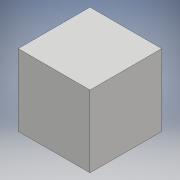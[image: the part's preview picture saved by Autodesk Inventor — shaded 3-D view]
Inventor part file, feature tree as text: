
AUTODESK INVENTOR PART (.ipt)
format: ipt  version: 2018 (Build 220112000, 112)  size: 83,968 bytes
history: native  units: mm
features: extrude x1, sketch x1
ambient origin geometry x8: Origin, YZ Plane, XZ Plane, XY Plane, X Axis, Y Axis, Z Axis, Center Point
bodies: Solid1 (feature_tree)
feature tree (2):
  extrude  "Extrusion1"  Depth=100.0mm
  sketch  "Sketch1"  dims[d0=100.0mm d1=100.0mm d2=100.0mm d3=0.0mm]
